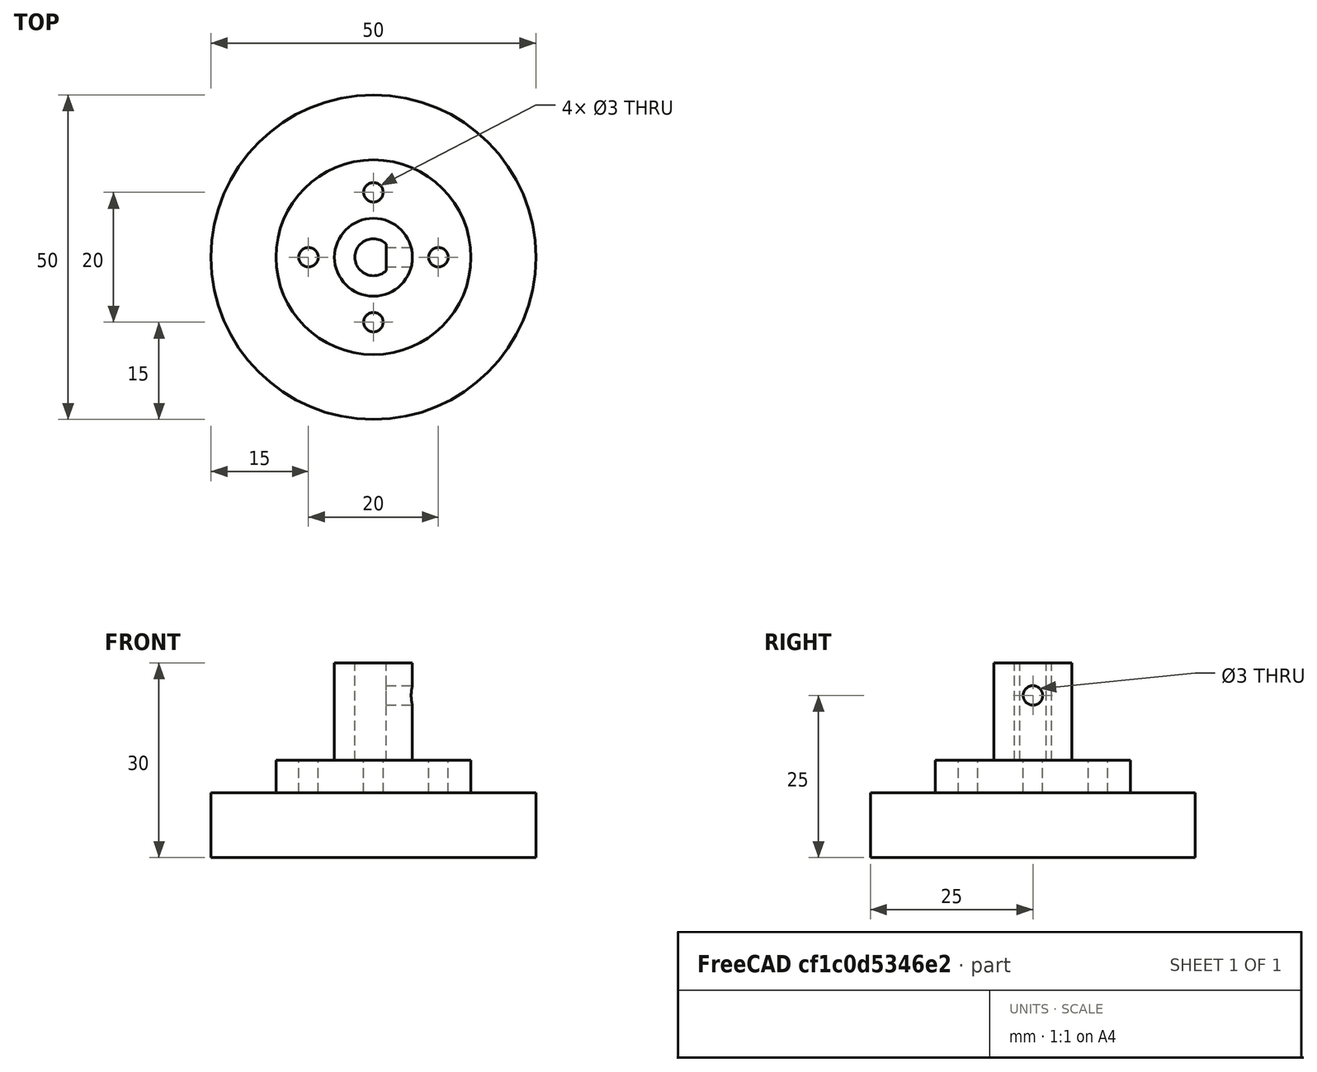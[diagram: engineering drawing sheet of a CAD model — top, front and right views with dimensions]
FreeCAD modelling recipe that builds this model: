
FCSTD DOCUMENT  (FreeCAD 0.16R6712 (Git))
Label: acomplemotor
License: All rights reserved
LicenseURL: http://en.wikipedia.org/wiki/All_rights_reserved
objects: Part::Cylinder×9, Part::Cut×9, Part::Box×1, Part::MultiFuse×1
note: 20 computed .brp shape members not serialized (recipe doc carries the construction recipe); baked Part::Feature solids carry a one-line shape summary decoded from their .brp

FEATURE [Part::Cylinder] Cylinder  label="Cilindro"
  Angle = 360
  Height = 5
  Radius = 15
FEATURE [Part::Cylinder] Cylinder001  label="tornillo 1"
  Angle = 360
  Height = 5
  Placement = pos=(10,0,0) rot=(0,0,1;0rad)
  Radius = 1.5
FEATURE [Part::Cylinder] Cylinder002  label="tornillo 2"
  Angle = 360
  Height = 5
  Placement = pos=(-10,0,0) rot=(0,0,1;0rad)
  Radius = 1.5
FEATURE [Part::Cylinder] Cylinder003  label="tornillo 3"
  Angle = 360
  Height = 5
  Placement = pos=(0,10,0) rot=(0,0,1;0rad)
  Radius = 1.5
FEATURE [Part::Cylinder] Cylinder004  label="tornillo 4"
  Angle = 360
  Height = 5
  Placement = pos=(0,-10,0) rot=(0,0,1;0rad)
  Radius = 1.5
FEATURE [Part::Cut] Cut
  Base = -> Cylinder
  Tool = -> Cylinder001
FEATURE [Part::Cut] Cut001
  Base = -> Cut
  Tool = -> Cylinder002
FEATURE [Part::Cut] Cut002
  Base = -> Cut001
  Tool = -> Cylinder003
FEATURE [Part::Cut] Cut003
  Base = -> Cut002
  Tool = -> Cylinder004
FEATURE [Part::Cylinder] Cylinder016  label="Cilindro003"
  Angle = 360
  Height = 15
  Placement = pos=(0,-186,0) rot=(0,0,1;0rad)
  Radius = 2.85
FEATURE [Part::Box] Box002  label="Cubo001"
  Height = 21
  Length = 11
  Placement = pos=(2,-191,-2) rot=(0,0,1;0rad)
  Width = 10
FEATURE [Part::Cut] Cut005
  Base = -> Cylinder016
  Tool = -> Box002
FEATURE [Part::Cut] Cut006
  Base = -> Box002
  Tool = -> Cylinder016
FEATURE [Part::Cut] Cut007
  Base = -> Cut005
  Placement = pos=(0,186,5) rot=(0,0,1;0rad)
  Tool = -> Cut006
FEATURE [Part::Cylinder] Cylinder017  label="Cilindro004"
  Angle = 360
  Height = 15
  Placement = pos=(0,0,5) rot=(0,0,1;0rad)
  Radius = 6
FEATURE [Part::Cut] Cut008
  Base = -> Cylinder017
  Tool = -> Cut007
FEATURE [Part::Cylinder] Cylinder018  label="Cilindro005"
  Angle = 360
  Height = 5
  Placement = pos=(1.45,0,15) rot=(0,1,0;1.5708rad)
  Radius = 1.5
FEATURE [Part::Cut] Cut009
  Base = -> Cut008
  Tool = -> Cylinder018
FEATURE [Part::Cylinder] Cylinder019  label="Cilindro006"
  Angle = 360
  Height = 10
  Placement = pos=(0,0,-10) rot=(0,0,1;0rad)
  Radius = 25
FEATURE [Part::MultiFuse] Fusion  label="Acople"
  Shapes = -> [Cut003,Cut009]
